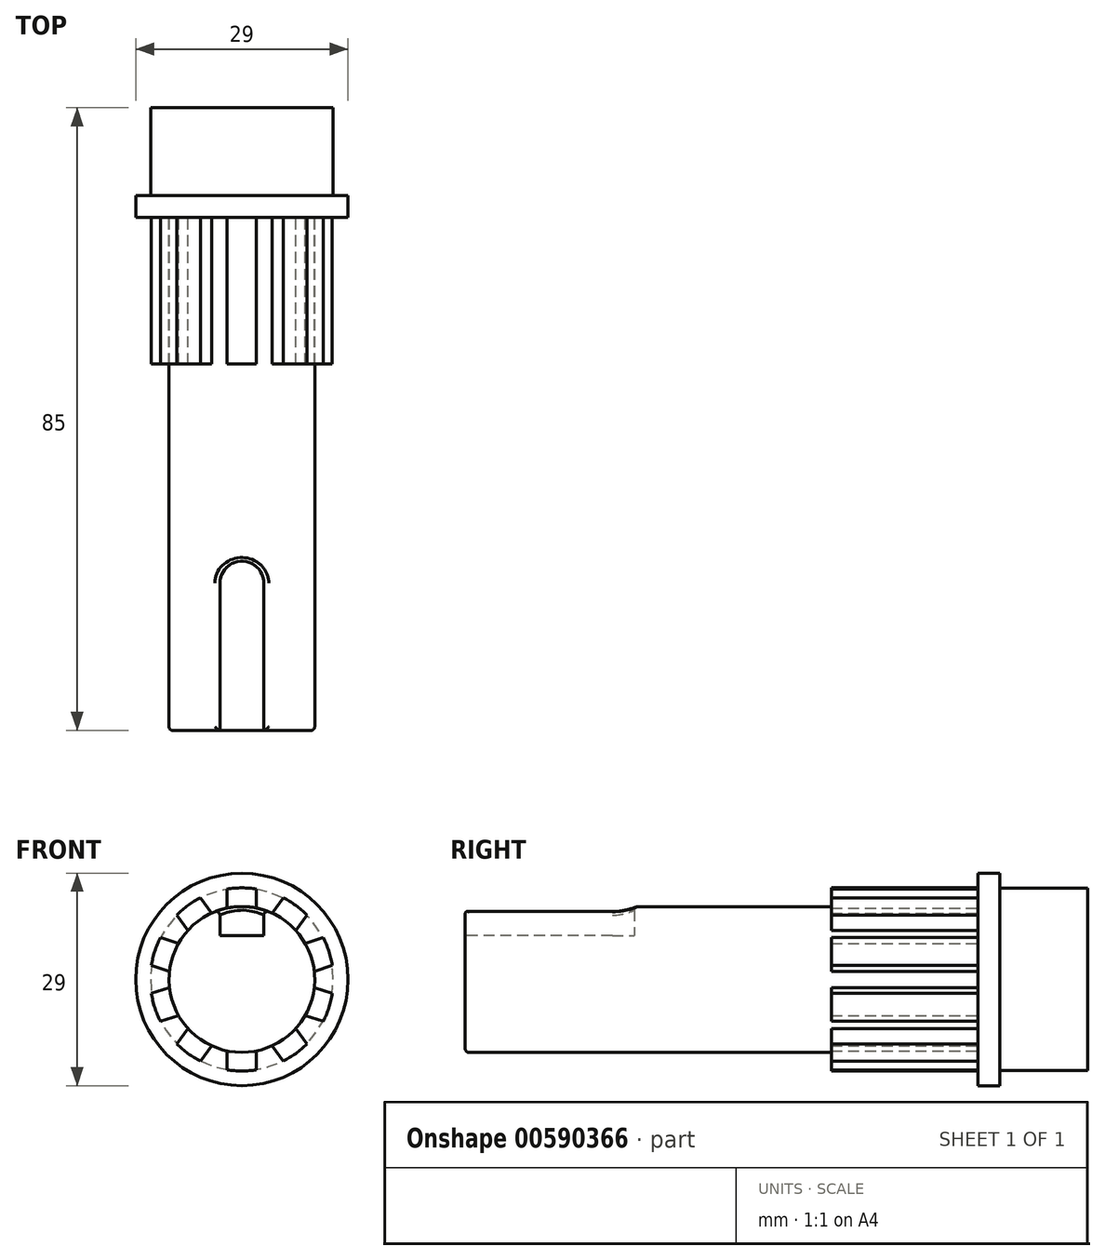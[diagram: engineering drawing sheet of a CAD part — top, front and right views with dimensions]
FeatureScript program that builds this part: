
annotation { "Feature Type Name" : "Feature", "Feature Type Description" : "" }
export const myFeature = defineFeature(function(context is Context, id is Id, definition is map)
    precondition{}
    {
        {
            var Q0;
            Q0=qCreatedBy(makeId("Front.planeOp"),FACE);
            var sketch = newSketch(context, id + "F0", { "sketchPlane" : qUnion([Q0])});
            skCircle(sketch, "E0", {"center": v(0, 0) * mm, "radius": 12.45 * mm});
            skSolve(sketch);
        }
        {
            var Q0;
            Q0=makeQuery(id+"F0.imprint","IMPRINT",FACE,{"disambiguationData":[TD([[makeQuery(id+"F0.imprint","IMPRINT",EDGE,{"derivedFrom":sQuery(id+"F0.wireOp",EDGE,"E0")}),1.0]])]});
            extrude(context, id + "F1", {"entities" : qUnion([Q0]), "oppositeDirection" : true, "depth" : 12 * mm, "offsetDistance" : 25 * mm});
        }
        {
            var Q0;
            Q0=qCreatedBy(makeId("Front.planeOp"),FACE);
            var sketch = newSketch(context, id + "F2", { "sketchPlane" : qUnion([Q0])});
            skCircle(sketch, "E1", {"center": v(0, 0) * mm, "radius": 14.5 * mm});
            skSolve(sketch);
        }
        {
            var Q0;
            Q0=makeQuery(id+"F2.imprint","IMPRINT",FACE,{"disambiguationData":[TD([[makeQuery(id+"F2.imprint","IMPRINT",EDGE,{"derivedFrom":sQuery(id+"F2.wireOp",EDGE,"E1")}),1.0]])]});
            extrude(context, id + "F3", {"entities" : qUnion([Q0]), "operationType" : NewBodyOperationType.ADD, "depth" : 3 * mm, "offsetDistance" : 25 * mm});
        }
        {
            var Q0;
            Q0=makeQuery(id+"F3.opExtrude","CAP_FACE",FACE,{"disambiguationData":[OSD([sQuery(id+"F2.wireOp",EDGE,"E1")])],"isStart":false});
            var sketch = newSketch(context, id + "F4", { "sketchPlane" : qUnion([Q0])});
            skCircle(sketch, "E2", {"center": v(0, 0) * mm, "radius": 9.95 * mm});
            skSolve(sketch);
        }
        {
            var Q0;
            Q0 = qSketchRegion(id + "F4", true);
            extrude(context, id + "F5", {"entities" : qUnion([Q0]), "operationType" : NewBodyOperationType.ADD, "depth" : 70 * mm, "offsetDistance" : 25 * mm});
        }
        {
            var Q0;
            Q0=makeQuery(id+"F3.opExtrude","CAP_FACE",FACE,{"disambiguationData":[OSD([sQuery(id+"F2.wireOp",EDGE,"E1")])],"isStart":false});
            var sketch = newSketch(context, id + "F6", { "sketchPlane" : qUnion([Q0])});
            skArc(sketch, "E3", {"start": v(2, 12.34) * mm, "mid": v(0, 12.5) * mm, "end": v(-2, 12.34) * mm});
            skLineSegment(sketch, "E4", {"start": v(-2, 12.34) * mm, "end": v(-2, 7.98) * mm});
            skLineSegment(sketch, "E5", {"start": v(-2, 7.98) * mm, "end": v(2, 7.98) * mm});
            skLineSegment(sketch, "E6", {"start": v(2, 7.98) * mm, "end": v(2, 12.34) * mm});
            skLineSegment(sketch, "E7.1.0", {"start": v(-8.87, 8.8) * mm, "end": v(-6.31, 5.28) * mm});
            skArc(sketch, "E7.1.1", {"start": v(-5.63, 11.16) * mm, "mid": v(-7.35, 10.11) * mm, "end": v(-8.87, 8.8) * mm});
            skLineSegment(sketch, "E7.1.2", {"start": v(-3.07, 7.63) * mm, "end": v(-5.63, 11.16) * mm});
            skLineSegment(sketch, "E7.1.3", {"start": v(-6.31, 5.28) * mm, "end": v(-3.07, 7.63) * mm});
            skLineSegment(sketch, "E7.2.0", {"start": v(-12.35, 1.91) * mm, "end": v(-8.2, 0.56) * mm});
            skArc(sketch, "E7.2.1", {"start": v(-11.12, 5.72) * mm, "mid": v(-11.89, 3.86) * mm, "end": v(-12.35, 1.91) * mm});
            skLineSegment(sketch, "E7.2.2", {"start": v(-6.97, 4.37) * mm, "end": v(-11.12, 5.72) * mm});
            skLineSegment(sketch, "E7.2.3", {"start": v(-8.2, 0.56) * mm, "end": v(-6.97, 4.37) * mm});
            skLineSegment(sketch, "E7.3.0", {"start": v(-11.12, -5.72) * mm, "end": v(-6.97, -4.37) * mm});
            skArc(sketch, "E7.3.1", {"start": v(-12.35, -1.91) * mm, "mid": v(-11.89, -3.86) * mm, "end": v(-11.12, -5.72) * mm});
            skLineSegment(sketch, "E7.3.2", {"start": v(-8.2, -0.56) * mm, "end": v(-12.35, -1.91) * mm});
            skLineSegment(sketch, "E7.3.3", {"start": v(-6.97, -4.37) * mm, "end": v(-8.2, -0.56) * mm});
            skLineSegment(sketch, "E7.4.0", {"start": v(-5.63, -11.16) * mm, "end": v(-3.07, -7.63) * mm});
            skArc(sketch, "E7.4.1", {"start": v(-8.87, -8.8) * mm, "mid": v(-7.35, -10.11) * mm, "end": v(-5.63, -11.16) * mm});
            skLineSegment(sketch, "E7.4.2", {"start": v(-6.31, -5.28) * mm, "end": v(-8.87, -8.8) * mm});
            skLineSegment(sketch, "E7.4.3", {"start": v(-3.07, -7.63) * mm, "end": v(-6.31, -5.28) * mm});
            skLineSegment(sketch, "E7.5.0", {"start": v(2, -12.34) * mm, "end": v(2, -7.98) * mm});
            skArc(sketch, "E7.5.1", {"start": v(-2, -12.34) * mm, "mid": v(0, -12.5) * mm, "end": v(2, -12.34) * mm});
            skLineSegment(sketch, "E7.5.2", {"start": v(-2, -7.98) * mm, "end": v(-2, -12.34) * mm});
            skLineSegment(sketch, "E7.5.3", {"start": v(2, -7.98) * mm, "end": v(-2, -7.98) * mm});
            skLineSegment(sketch, "E7.6.0", {"start": v(8.87, -8.8) * mm, "end": v(6.31, -5.28) * mm});
            skArc(sketch, "E7.6.1", {"start": v(5.63, -11.16) * mm, "mid": v(7.35, -10.11) * mm, "end": v(8.87, -8.8) * mm});
            skLineSegment(sketch, "E7.6.2", {"start": v(3.07, -7.63) * mm, "end": v(5.63, -11.16) * mm});
            skLineSegment(sketch, "E7.6.3", {"start": v(6.31, -5.28) * mm, "end": v(3.07, -7.63) * mm});
            skLineSegment(sketch, "E7.7.0", {"start": v(12.35, -1.91) * mm, "end": v(8.2, -0.56) * mm});
            skArc(sketch, "E7.7.1", {"start": v(11.12, -5.72) * mm, "mid": v(11.89, -3.86) * mm, "end": v(12.35, -1.91) * mm});
            skLineSegment(sketch, "E7.7.2", {"start": v(6.97, -4.37) * mm, "end": v(11.12, -5.72) * mm});
            skLineSegment(sketch, "E7.7.3", {"start": v(8.2, -0.56) * mm, "end": v(6.97, -4.37) * mm});
            skLineSegment(sketch, "E7.8.0", {"start": v(11.12, 5.72) * mm, "end": v(6.97, 4.37) * mm});
            skArc(sketch, "E7.8.1", {"start": v(12.35, 1.91) * mm, "mid": v(11.89, 3.86) * mm, "end": v(11.12, 5.72) * mm});
            skLineSegment(sketch, "E7.8.2", {"start": v(8.2, 0.56) * mm, "end": v(12.35, 1.91) * mm});
            skLineSegment(sketch, "E7.8.3", {"start": v(6.97, 4.37) * mm, "end": v(8.2, 0.56) * mm});
            skLineSegment(sketch, "E7.9.0", {"start": v(5.63, 11.16) * mm, "end": v(3.07, 7.63) * mm});
            skArc(sketch, "E7.9.1", {"start": v(8.87, 8.8) * mm, "mid": v(7.35, 10.11) * mm, "end": v(5.63, 11.16) * mm});
            skLineSegment(sketch, "E7.9.2", {"start": v(6.31, 5.28) * mm, "end": v(8.87, 8.8) * mm});
            skLineSegment(sketch, "E7.9.3", {"start": v(3.07, 7.63) * mm, "end": v(6.31, 5.28) * mm});
            skSolve(sketch);
        }
        {
            var Q0;
            {var subQ0=sQuery(id+"F6.wireOp",EDGE,"E3");Q0=makeQuery(id+"F6.imprint","IMPRINT",FACE,{"disambiguationData":[TD([[makeQuery(id+"F6.imprint","IMPRINT",EDGE,{"derivedFrom":subQ0}),1.0]])]});}
            var Q1;
            {var subQ0=sQuery(id+"F6.wireOp",EDGE,"E7.1.1");Q1=makeQuery(id+"F6.imprint","IMPRINT",FACE,{"disambiguationData":[TD([[makeQuery(id+"F6.imprint","IMPRINT",EDGE,{"derivedFrom":subQ0}),1.0]])]});}
            var Q2;
            {var subQ0=sQuery(id+"F6.wireOp",EDGE,"E7.2.1");Q2=makeQuery(id+"F6.imprint","IMPRINT",FACE,{"disambiguationData":[TD([[makeQuery(id+"F6.imprint","IMPRINT",EDGE,{"derivedFrom":subQ0}),1.0]])]});}
            var Q3;
            {var subQ0=sQuery(id+"F6.wireOp",EDGE,"E7.3.1");Q3=makeQuery(id+"F6.imprint","IMPRINT",FACE,{"disambiguationData":[TD([[makeQuery(id+"F6.imprint","IMPRINT",EDGE,{"derivedFrom":subQ0}),1.0]])]});}
            var Q4;
            {var subQ0=sQuery(id+"F6.wireOp",EDGE,"E7.4.1");Q4=makeQuery(id+"F6.imprint","IMPRINT",FACE,{"disambiguationData":[TD([[makeQuery(id+"F6.imprint","IMPRINT",EDGE,{"derivedFrom":subQ0}),1.0]])]});}
            var Q5;
            {var subQ0=sQuery(id+"F6.wireOp",EDGE,"E7.5.1");Q5=makeQuery(id+"F6.imprint","IMPRINT",FACE,{"disambiguationData":[TD([[makeQuery(id+"F6.imprint","IMPRINT",EDGE,{"derivedFrom":subQ0}),1.0]])]});}
            var Q6;
            {var subQ0=sQuery(id+"F6.wireOp",EDGE,"E7.6.1");Q6=makeQuery(id+"F6.imprint","IMPRINT",FACE,{"disambiguationData":[TD([[makeQuery(id+"F6.imprint","IMPRINT",EDGE,{"derivedFrom":subQ0}),1.0]])]});}
            var Q7;
            {var subQ0=sQuery(id+"F6.wireOp",EDGE,"E7.7.1");Q7=makeQuery(id+"F6.imprint","IMPRINT",FACE,{"disambiguationData":[TD([[makeQuery(id+"F6.imprint","IMPRINT",EDGE,{"derivedFrom":subQ0}),1.0]])]});}
            var Q8;
            {var subQ0=sQuery(id+"F6.wireOp",EDGE,"E7.8.1");Q8=makeQuery(id+"F6.imprint","IMPRINT",FACE,{"disambiguationData":[TD([[makeQuery(id+"F6.imprint","IMPRINT",EDGE,{"derivedFrom":subQ0}),1.0]])]});}
            var Q9;
            {var subQ0=sQuery(id+"F6.wireOp",EDGE,"E7.9.1");Q9=makeQuery(id+"F6.imprint","IMPRINT",FACE,{"disambiguationData":[TD([[makeQuery(id+"F6.imprint","IMPRINT",EDGE,{"derivedFrom":subQ0}),1.0]])]});}
            extrude(context, id + "F7", {"entities" : qUnion([Q0, Q1, Q2, Q3, Q4, Q5, Q6, Q7, Q8, Q9]), "operationType" : NewBodyOperationType.ADD, "depth" : 20 * mm, "offsetDistance" : 25 * mm});
        }
        {
            var Q0;
            Q0=qCreatedBy(makeId("Top.planeOp"),FACE);
            cPlane(context, id + "F8", {"entities" : qUnion([Q0]), "cplaneType" : CPlaneType.OFFSET, "offset" : 6 * mm, "width" : 150 * mm, "height" : 150 * mm});
        }
        {
            var Q0;
            Q0=qCreatedBy(id+"F8.planeOp",FACE);
            var sketch = newSketch(context, id + "F9", { "sketchPlane" : qUnion([Q0])});
            skLineSegment(sketch, "E8.top", {"start": v(-3, -80.14) * mm, "end": v(3, -80.14) * mm});
            skLineSegment(sketch, "E8.left", {"start": v(-3, -52.9) * mm, "end": v(-3, -80.14) * mm});
            skLineSegment(sketch, "E8.right", {"start": v(3, -52.9) * mm, "end": v(3, -80.14) * mm});
            skArc(sketch, "E9", {"start": v(3, -52.9) * mm, "mid": v(0, -49.9) * mm, "end": v(-3, -52.9) * mm});
            skSolve(sketch);
        }
        {
            var Q0;
            Q0=makeQuery(id+"F9.imprint","IMPRINT",FACE,{"disambiguationData":[TD([[makeQuery(id+"F9.imprint","IMPRINT",EDGE,{"derivedFrom":sQuery(id+"F9.wireOp",EDGE,"E8.top")}),1.0]])]});
            extrude(context, id + "F10", {"entities" : qUnion([Q0]), "operationType" : NewBodyOperationType.REMOVE, "depth" : 23.8 * mm, "offsetDistance" : 25 * mm});
        }
        {
            var Q0;
            Q0=makeQuery(id+"F10.boolean.opBoolean","INTERSECT",EDGE,{"derivedFrom":[makeQuery(id+"F5.opExtrude","SWEPT_FACE",FACE,{"disambiguationData":[OSD([sQuery(id+"F4.wireOp",EDGE,"E2")])]}),makeQuery(id+"F10.opExtrude","SWEPT_FACE",FACE,{"disambiguationData":[OSD([sQuery(id+"F9.wireOp",EDGE,"E8.left")])]})]});
            var Q1;
            Q1=makeQuery(id+"F10.boolean.opBoolean","INTERSECT",EDGE,{"derivedFrom":[makeQuery(id+"F5.opExtrude","SWEPT_FACE",FACE,{"disambiguationData":[OSD([sQuery(id+"F4.wireOp",EDGE,"E2")])]}),makeQuery(id+"F10.opExtrude","SWEPT_FACE",FACE,{"disambiguationData":[OSD([sQuery(id+"F9.wireOp",EDGE,"E9")])]})]});
            var Q2;
            Q2=makeQuery(id+"F10.boolean.opBoolean","INTERSECT",EDGE,{"derivedFrom":[makeQuery(id+"F5.opExtrude","SWEPT_FACE",FACE,{"disambiguationData":[OSD([sQuery(id+"F4.wireOp",EDGE,"E2")])]}),makeQuery(id+"F10.opExtrude","SWEPT_FACE",FACE,{"disambiguationData":[OSD([sQuery(id+"F9.wireOp",EDGE,"E8.right")])]})]});
            var Q3;
            Q3=makeQuery(id+"F5.opExtrude","CAP_EDGE",EDGE,{"disambiguationData":[OSD([sQuery(id+"F4.wireOp",EDGE,"E2")])],"isStart":false});
            fillet(context, id + "F11", {"entities" : qUnion([Q0, Q1, Q2, Q3]), "radius" : 0.5 * mm, "tangentPropagation" : true, "allowEdgeOverflow" : false});
        }
    });
